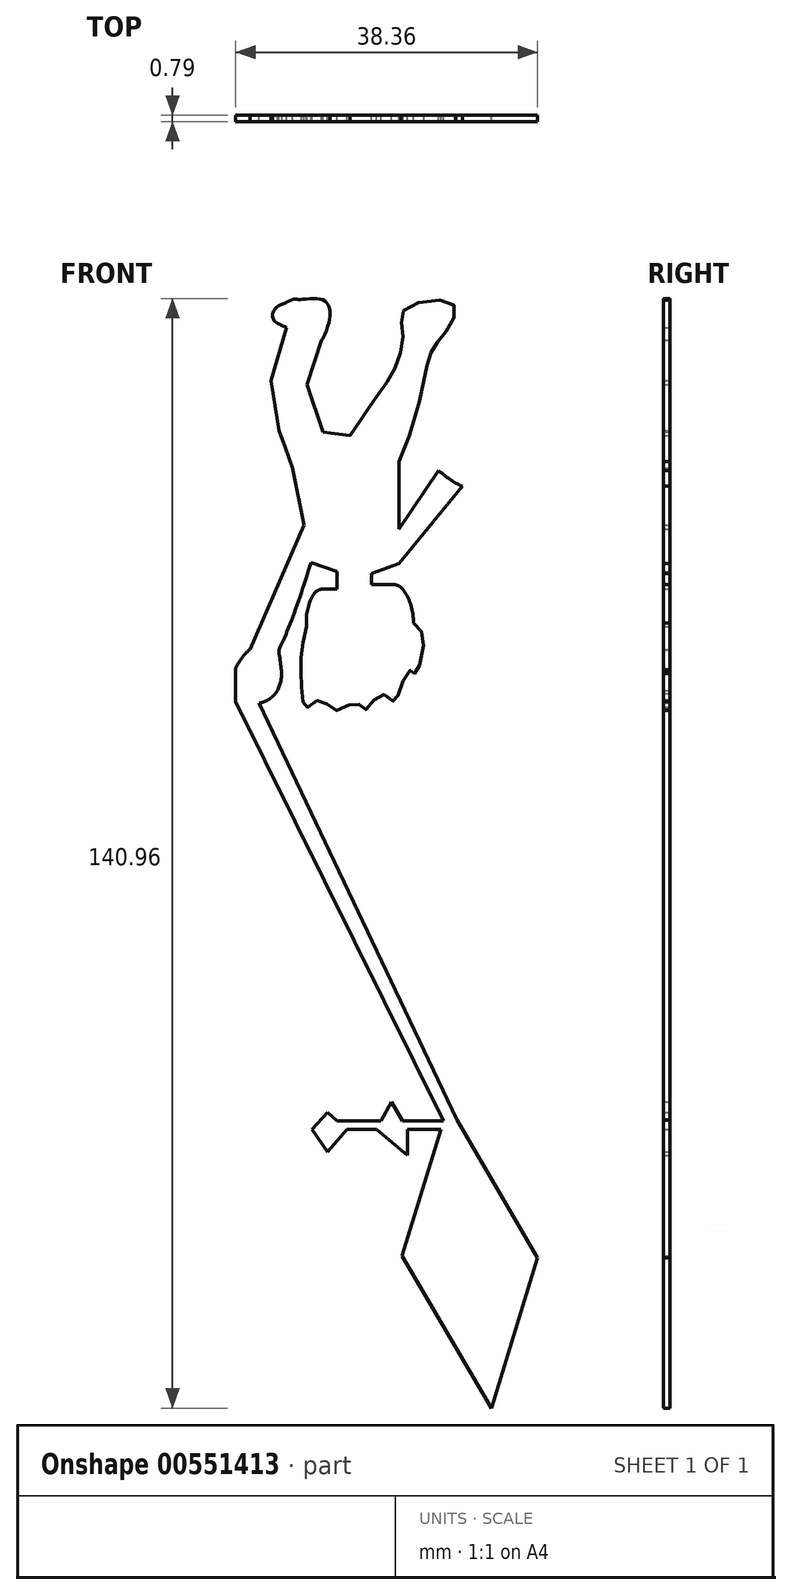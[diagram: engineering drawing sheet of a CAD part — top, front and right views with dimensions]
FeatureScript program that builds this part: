
annotation { "Feature Type Name" : "Feature", "Feature Type Description" : "" }
export const myFeature = defineFeature(function(context is Context, id is Id, definition is map)
    precondition{}
    {
        {
            var Q0;
            Q0=qCreatedBy(makeId("Front.planeOp"),FACE);
            var sketch = newSketch(context, id + "F0", { "sketchPlane" : qUnion([Q0])});
            skLineSegment(sketch, "E0.bottom", {"start": v(-6.99, 61.61) * mm, "end": v(6.77, 59.71) * mm});
            skLineSegment(sketch, "E0.right", {"start": v(31.69, 46.53) * mm, "end": v(31.69, 12.34) * mm});
            skEllipticalArc(sketch, "E1", {});
            skEllipticalArc(sketch, "E2", {});
            skLineSegment(sketch, "E3.left", {"start": v(-51.29, -58.62) * mm, "end": v(-51.29, -75.42) * mm});
            skArc(sketch, "E4", {"start": v(39, -35.56) * mm, "mid": v(37.85, -26.62) * mm, "end": v(33.85, -18.55) * mm});
            skFitSpline(sketch, "E5", {"points": [v(39, -35.56) * mm, v(44.2, -43.53) * mm, v(39.99, -61.25) * mm, v(38.36, -59.43) * mm, v(32.94, -67.25) * mm, v(29.18, -75.32) * mm, v(22.36, -71.7) * mm, v(14.7, -79.56) * mm, v(10.05, -76.04) * mm, v(-0.34, -79.97) * mm, v(-8.26, -74.57) * mm, v(-15.43, -78.48) * mm, v(-17.58, -70.09) * mm, v(-18.13, -54.53) * mm, v(-15.24, -37.3) * mm], "startDerivative": vector(117.5, -103.15) * mm, "endDerivative": vector(46.93, 196.09) * mm});
            skPoint(sketch, "E6.center.orphan", {"position": v(48.43, 93.24) * mm});
            skArc(sketch, "E7.trimOffspring", {"start": v(-12.04, -21.43) * mm, "mid": v(-14.85, -29.12) * mm, "end": v(-15.24, -37.3) * mm});
            skLineSegment(sketch, "E8.top", {"start": v(-7.6, 108.33) * mm, "end": v(-7.6, 108.33) * mm});
            skLineSegment(sketch, "E9", {"start": v(64.06, -292.9) * mm, "end": v(102.17, -357.96) * mm});
            skLineSegment(sketch, "E10", {"start": v(102.17, -357.96) * mm, "end": v(78.66, -434.5) * mm});
            skLineSegment(sketch, "E11", {"start": v(78.66, -434.5) * mm, "end": v(33.32, -357.09) * mm});
            skLineSegment(sketch, "E12", {"start": v(33.32, -357.09) * mm, "end": v(53.04, -292.9) * mm});
            skLineSegment(sketch, "E13", {"start": v(53.04, -292.9) * mm, "end": v(36.13, -292.9) * mm});
            skLineSegment(sketch, "E14", {"start": v(-12.5, -292.9) * mm, "end": v(-4.7, -284.05) * mm});
            skLineSegment(sketch, "E15", {"start": v(-4.7, -284.05) * mm, "end": v(0.33, -288.48) * mm});
            skLineSegment(sketch, "E16", {"start": v(5.35, -292.9) * mm, "end": v(-4.7, -304.28) * mm});
            skLineSegment(sketch, "E17", {"start": v(-4.7, -304.28) * mm, "end": v(-12.5, -292.9) * mm});
            skLineSegment(sketch, "E18", {"start": v(22.63, -288.48) * mm, "end": v(27.82, -278.76) * mm});
            skLineSegment(sketch, "E19", {"start": v(27.82, -278.76) * mm, "end": v(33.5, -288.42) * mm});
            skLineSegment(sketch, "E20", {"start": v(36.13, -292.9) * mm, "end": v(36.13, -306.08) * mm});
            skLineSegment(sketch, "E21", {"start": v(36.13, -306.08) * mm, "end": v(20.27, -292.9) * mm});
            skPoint(sketch, "E22.endSnap0", {"position": v(49.11, -316.57) * mm});
            skLineSegment(sketch, "E23.trimOffspring", {"start": v(20.27, -292.9) * mm, "end": v(5.35, -292.9) * mm});
            skLineSegment(sketch, "E24.trimOffspring", {"start": v(22.63, -288.48) * mm, "end": v(0.33, -288.48) * mm});
            skPoint(sketch, "E25.orphan", {"position": v(-8.6, -288.48) * mm});
            skLineSegment(sketch, "E26", {"start": v(64.06, -292.9) * mm, "end": v(61.18, -288) * mm});
            skLineSegment(sketch, "E27", {"start": v(33.5, -288.42) * mm, "end": v(54.42, -288.42) * mm});
            skLineSegment(sketch, "E28", {"start": v(61.18, -288) * mm, "end": v(-39.3, -76.21) * mm});
            skLineSegment(sketch, "E29", {"start": v(-51.29, -75.42) * mm, "end": v(54.42, -288.42) * mm});
            skPoint(sketch, "E30.centerSnap0", {"position": v(31.69, 15.3) * mm});
            skFitSpline(sketch, "E31", {"points": [v(31.69, 46.53) * mm, v(36.9, 59.71) * mm, v(44, 85.87) * mm, v(48.43, 102.96) * mm, v(56.02, 113.33) * mm, v(59.17, 126.67) * mm, v(34.72, 124.02) * mm, v(33.59, 112.13) * mm, v(29.18, 93.24) * mm, v(18.78, 77.49) * mm, v(6.77, 59.71) * mm], "startDerivative": vector(58.15, 168.6) * mm, "endDerivative": vector(-134.01, -174.77) * mm});
            skPoint(sketch, "E32.visualSharp", {"position": v(-1.24, 108.33) * mm});
            skLineSegment(sketch, "E33", {"start": v(-29.2, 62.27) * mm, "end": v(-33.25, 87.78) * mm});
            skPoint(sketch, "E34.visualSharp", {"position": v(-1.24, 129.87) * mm});
            skPoint(sketch, "E35.visualSharp", {"position": v(-26.04, 127.16) * mm});
            skLineSegment(sketch, "E36.bottom", {"start": v(31.69, -5.28) * mm, "end": v(63.94, 34.11) * mm});
            skLineSegment(sketch, "E36.top", {"start": v(31.69, 12.34) * mm, "end": v(51.7, 41.92) * mm});
            skPoint(sketch, "E37.visualSharp", {"position": v(-28.26, -76.47) * mm});
            skArc(sketch, "E37.filletArc", {"start": v(-39.3, -76.21) * mm, "mid": v(-34.02, -74) * mm, "end": v(-30.07, -69.84) * mm});
            skLineSegment(sketch, "E38", {"start": v(-16.6, 14.37) * mm, "end": v(-44.05, -48.84) * mm});
            skFitSpline(sketch, "E39", {"points": [v(-29.32, -49.25) * mm, v(-28, -62.36) * mm, v(-30.07, -69.84) * mm], "startDerivative": vector(1.6, -23.12) * mm, "endDerivative": vector(-5.97, -15.6) * mm});
            skLineSegment(sketch, "E40", {"start": v(31.69, -5.28) * mm, "end": v(17.67, -10.3) * mm});
            skLineSegment(sketch, "E41", {"start": v(0.14, -9.25) * mm, "end": v(-13.11, -4.83) * mm});
            skLineSegment(sketch, "E42", {"start": v(0.14, -9.25) * mm, "end": v(0.14, -18.13) * mm});
            skLineSegment(sketch, "E43", {"start": v(17.67, -15.93) * mm, "end": v(17.67, -10.3) * mm});
            skLineSegment(sketch, "E44", {"start": v(28.7, -15.93) * mm, "end": v(17.67, -15.93) * mm});
            skLineSegment(sketch, "E45", {"start": v(-6.47, -18.13) * mm, "end": v(0.14, -18.13) * mm});
            skPoint(sketch, "E46.visualSharp", {"position": v(31.69, -15.93) * mm});
            skArc(sketch, "E46.filletArc", {"start": v(33.85, -18.55) * mm, "mid": v(31.6, -16.62) * mm, "end": v(28.7, -15.93) * mm});
            skPoint(sketch, "E47.visualSharp", {"position": v(-9.9, -18.13) * mm});
            skArc(sketch, "E47.filletArc", {"start": v(-6.47, -18.13) * mm, "mid": v(-9.7, -19.02) * mm, "end": v(-12.04, -21.43) * mm});
            skFitSpline(sketch, "E48", {"points": [v(63.94, 34.11) * mm, v(66.93, 35.96) * mm, v(71.37, 41.45) * mm, v(74.13, 50.7) * mm, v(71.31, 59.88) * mm, v(63.94, 61.15) * mm, v(56.6, 55.94) * mm, v(54.84, 53.05) * mm, v(53.9, 57.66) * mm, v(51.26, 61.8) * mm, v(49.04, 60.16) * mm, v(49.45, 44.57) * mm, v(51.7, 41.92) * mm, v(63.94, 34.11) * mm]});
            skLineSegment(sketch, "E49", {"start": v(-7.6, 108.33) * mm, "end": v(-15.05, 85.69) * mm});
            skLineSegment(sketch, "E50", {"start": v(-15.05, 85.69) * mm, "end": v(-6.99, 61.61) * mm});
            skLineSegment(sketch, "E51", {"start": v(-33.25, 87.78) * mm, "end": v(-25.33, 114.68) * mm});
            skLineSegment(sketch, "E52", {"start": v(-28.2, 126.36) * mm, "end": v(-24.56, 127.92) * mm});
            skLineSegment(sketch, "E53", {"start": v(-18.58, 128.94) * mm, "end": v(-18.42, 128.94) * mm});
            skFitSpline(sketch, "E54", {"points": [v(-25.33, 114.68) * mm, v(-32.17, 119.02) * mm, v(-31.47, 123.9) * mm, v(-28.2, 126.36) * mm, v(-26.04, 127.16) * mm, v(-22.18, 128.94) * mm, v(-18.42, 128.94) * mm, v(-7.58, 128.94) * mm, v(-3.78, 125.05) * mm, v(-3.78, 117.84) * mm, v(-7.6, 108.33) * mm, v(-7.6, 114.68) * mm], "startDerivative": vector(-82.54, 33.68) * mm, "endDerivative": vector(9.21, 102.4) * mm});
            skLineSegment(sketch, "E55", {"start": v(-16.6, 14.37) * mm, "end": v(-22.32, 43.16) * mm});
            skLineSegment(sketch, "E56", {"start": v(-22.32, 43.16) * mm, "end": v(-26.03, 53.39) * mm});
            skLineSegment(sketch, "E57", {"start": v(-26.03, 53.39) * mm, "end": v(-29.2, 62.27) * mm});
            const initialGuessF0  = {"E1": [-0.022339077437918624, 0.003175500664243349, -0.2719348993949449, -0.9623156501330846, 0.07140757582628088, 0.011084038187954698, 0.7479317708624716, 1.4980100655150421], "E2": [-0.041757289386275216, -0.06554112709145166, -0.3420601443203688, -0.9396780606503106, 0.020509634080830817, 0.011467318252549749, 3.89836427042406, 4.553743065203518]};
            skSetInitialGuess(sketch, initialGuessF0);
            skSolve(sketch);
        }
        {
            var Q0;
            Q0=makeQuery(id+"F0.imprint","IMPRINT",FACE,{"disambiguationData":[TD([[makeQuery(id+"F0.imprint","IMPRINT",EDGE,{"derivedFrom":sQuery(id+"F0.wireOp",EDGE,"E0.bottom")}),-1.0]])]});
            extrude(context, id + "F1", {"entities" : qUnion([Q0]), "depth" : 3.17 * mm, "offsetDistance" : 25.4 * mm});
        }
        {
            var Q0;
            Q0=makeQuery(id+"F1.opExtrude","SWEPT_BODY",BODY,{"disambiguationData":[OSD([sQuery(id+"F0.wireOp",EDGE,"E0.bottom"),sQuery(id+"F0.wireOp",EDGE,"E0.right"),sQuery(id+"F0.wireOp",EDGE,"E1"),sQuery(id+"F0.wireOp",EDGE,"E2"),sQuery(id+"F0.wireOp",EDGE,"E3.left"),sQuery(id+"F0.wireOp",EDGE,"E4"),sQuery(id+"F0.wireOp",EDGE,"E5"),sQuery(id+"F0.wireOp",EDGE,"E7.trimOffspring"),sQuery(id+"F0.wireOp",EDGE,"E9"),sQuery(id+"F0.wireOp",EDGE,"E10"),sQuery(id+"F0.wireOp",EDGE,"E11"),sQuery(id+"F0.wireOp",EDGE,"E12"),sQuery(id+"F0.wireOp",EDGE,"E13"),sQuery(id+"F0.wireOp",EDGE,"E14"),sQuery(id+"F0.wireOp",EDGE,"E15"),sQuery(id+"F0.wireOp",EDGE,"E16"),sQuery(id+"F0.wireOp",EDGE,"E17"),sQuery(id+"F0.wireOp",EDGE,"E18"),sQuery(id+"F0.wireOp",EDGE,"E19"),sQuery(id+"F0.wireOp",EDGE,"E20"),sQuery(id+"F0.wireOp",EDGE,"E21"),sQuery(id+"F0.wireOp",EDGE,"E23.trimOffspring"),sQuery(id+"F0.wireOp",EDGE,"E24.trimOffspring"),sQuery(id+"F0.wireOp",EDGE,"E26"),sQuery(id+"F0.wireOp",EDGE,"E27"),sQuery(id+"F0.wireOp",EDGE,"E28"),sQuery(id+"F0.wireOp",EDGE,"E29"),sQuery(id+"F0.wireOp",EDGE,"E31"),sQuery(id+"F0.wireOp",EDGE,"E33"),sQuery(id+"F0.wireOp",EDGE,"E36.bottom"),sQuery(id+"F0.wireOp",EDGE,"E36.top"),sQuery(id+"F0.wireOp",EDGE,"E37.filletArc"),sQuery(id+"F0.wireOp",EDGE,"E38"),sQuery(id+"F0.wireOp",EDGE,"E39"),sQuery(id+"F0.wireOp",EDGE,"E40"),sQuery(id+"F0.wireOp",EDGE,"E41"),sQuery(id+"F0.wireOp",EDGE,"E42"),sQuery(id+"F0.wireOp",EDGE,"E43"),sQuery(id+"F0.wireOp",EDGE,"E44"),sQuery(id+"F0.wireOp",EDGE,"E45"),sQuery(id+"F0.wireOp",EDGE,"E46.filletArc"),sQuery(id+"F0.wireOp",EDGE,"E47.filletArc"),sQuery(id+"F0.wireOp",EDGE,"E48"),sQuery(id+"F0.wireOp",EDGE,"E49"),sQuery(id+"F0.wireOp",EDGE,"E50"),sQuery(id+"F0.wireOp",EDGE,"E51"),sQuery(id+"F0.wireOp",EDGE,"E52"),sQuery(id+"F0.wireOp",EDGE,"E54"),sQuery(id+"F0.wireOp",EDGE,"E54"),sQuery(id+"F0.wireOp",EDGE,"E55"),sQuery(id+"F0.wireOp",EDGE,"E56"),sQuery(id+"F0.wireOp",EDGE,"E57")])]});
            var Q1;
            Q1=sQuery(id+"F0.wireOp",VERTEX,"E7.trimOffspring.center");
            transform(context, id + "F2", {"entities" : qUnion([Q0]), "transformType" : TransformType.SCALE_UNIFORMLY, "scale" : .25, "scalePoint" : qUnion([Q1]), "makeCopy" : false});
        }
    });
